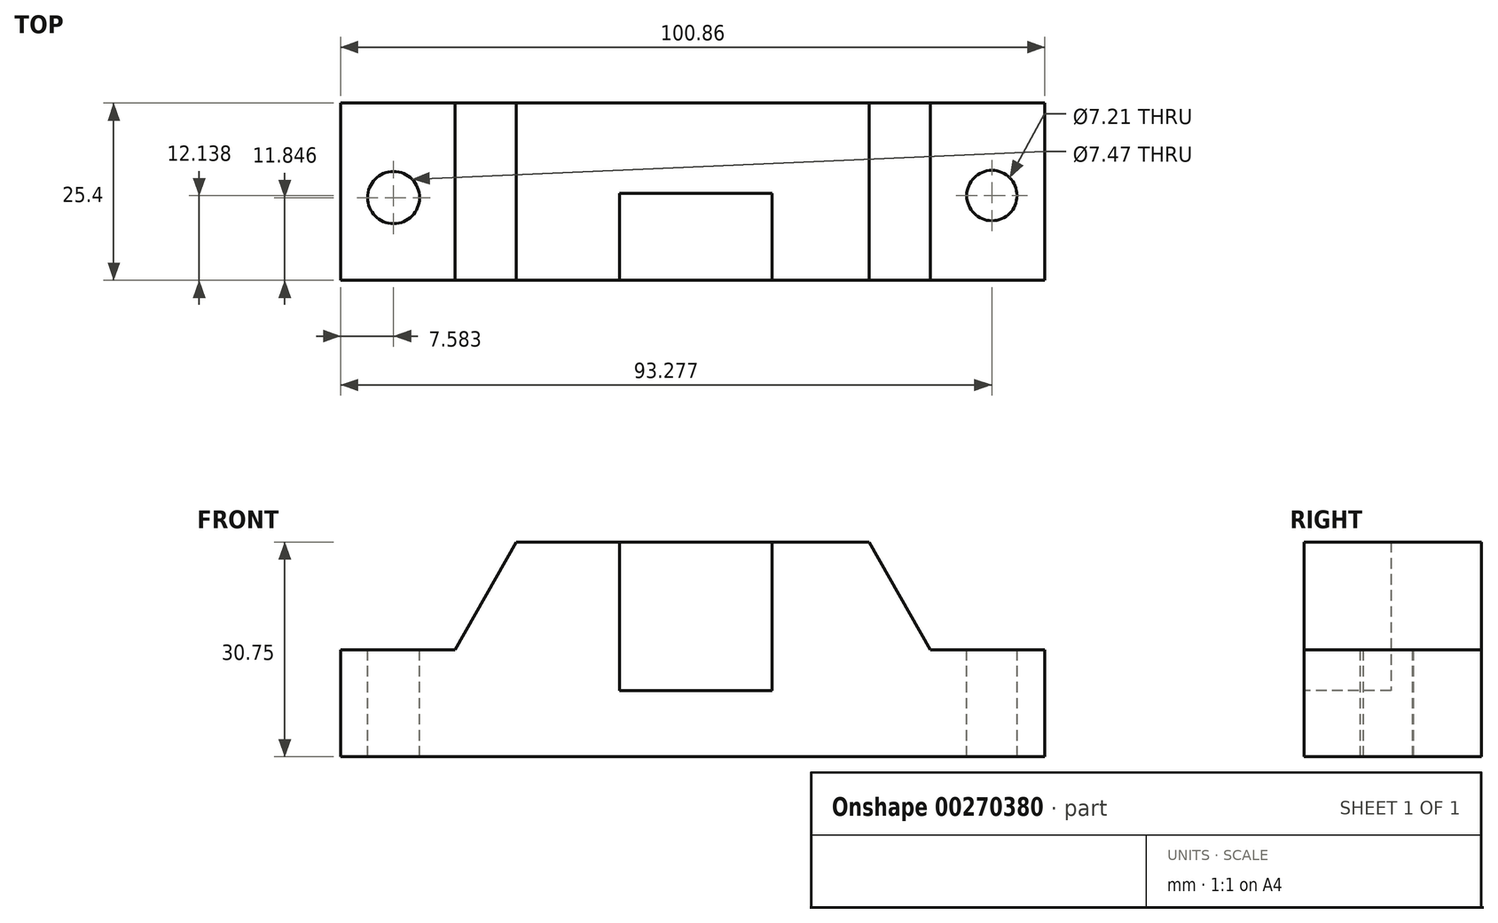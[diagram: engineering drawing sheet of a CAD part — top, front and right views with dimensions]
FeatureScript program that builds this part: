
annotation { "Feature Type Name" : "Feature", "Feature Type Description" : "" }
export const myFeature = defineFeature(function(context is Context, id is Id, definition is map)
    precondition{}
    {
        {
            var Q0;
            Q0=qCreatedBy(makeId("Front.planeOp"),FACE);
            var sketch = newSketch(context, id + "F0", { "sketchPlane" : qUnion([Q0])});
            skLineSegment(sketch, "E0", {"start": v(0, 30.75) * mm, "end": v(25.28, 30.75) * mm});
            skLineSegment(sketch, "E1", {"start": v(25.28, 30.75) * mm, "end": v(34.03, 15.3) * mm});
            skLineSegment(sketch, "E2", {"start": v(34.03, 15.3) * mm, "end": v(50.43, 15.3) * mm});
            skLineSegment(sketch, "E3", {"start": v(50.43, 15.3) * mm, "end": v(50.43, 0) * mm});
            skLineSegment(sketch, "E4", {"start": v(50.43, 0) * mm, "end": v(0, 0) * mm});
            skLineSegment(sketch, "E5", {"start": v(0, 0) * mm, "end": v(0, 30.75) * mm});
            skLineSegment(sketch, "E6.MirrorCS", {"start": v(0, 30.75) * mm, "end": v(-25.28, 30.75) * mm});
            skLineSegment(sketch, "E7.MirrorCS", {"start": v(-25.28, 30.75) * mm, "end": v(-34.03, 15.3) * mm});
            skLineSegment(sketch, "E8.MirrorCS", {"start": v(-34.03, 15.3) * mm, "end": v(-50.43, 15.3) * mm});
            skLineSegment(sketch, "E9.MirrorCS", {"start": v(-50.43, 15.3) * mm, "end": v(-50.43, 0) * mm});
            skLineSegment(sketch, "E10.MirrorCS", {"start": v(-50.43, 0) * mm, "end": v(0, 0) * mm});
            skSolve(sketch);
        }
        {
            var Q0;
            Q0 = qSketchRegion(id + "F0", true);
            extrude(context, id + "F1", {"entities" : qUnion([Q0]), "depth" : 25.4 * mm});
        }
        {
            var Q0;
            Q0=makeQuery(id+"F1.opExtrude","CAP_FACE",FACE,{"disambiguationData":[OSD([sQuery(id+"F0.wireOp",EDGE,"E0"),sQuery(id+"F0.wireOp",EDGE,"E1"),sQuery(id+"F0.wireOp",EDGE,"E2"),sQuery(id+"F0.wireOp",EDGE,"E3"),sQuery(id+"F0.wireOp",EDGE,"E4"),sQuery(id+"F0.wireOp",EDGE,"E6.MirrorCS"),sQuery(id+"F0.wireOp",EDGE,"E7.MirrorCS"),sQuery(id+"F0.wireOp",EDGE,"E8.MirrorCS"),sQuery(id+"F0.wireOp",EDGE,"E9.MirrorCS"),sQuery(id+"F0.wireOp",EDGE,"E10.MirrorCS")])],"isStart":false});
            var sketch = newSketch(context, id + "F2", { "sketchPlane" : qUnion([Q0])});
            skLineSegment(sketch, "E11", {"start": v(-10.5, 31.92) * mm, "end": v(-10.5, 9.47) * mm});
            skLineSegment(sketch, "E12", {"start": v(-10.5, 9.47) * mm, "end": v(11.37, 9.47) * mm});
            skLineSegment(sketch, "E13", {"start": v(11.37, 9.47) * mm, "end": v(11.37, 31.92) * mm});
            skLineSegment(sketch, "E14", {"start": v(-10.5, 31.92) * mm, "end": v(11.37, 31.92) * mm});
            skSolve(sketch);
        }
        {
            var Q0;
            Q0 = qSketchRegion(id + "F2", true);
            extrude(context, id + "F3", {"entities" : qUnion([Q0]), "operationType" : NewBodyOperationType.REMOVE, "oppositeDirection" : true, "depth" : 12.45 * mm});
        }
        {
            var Q0;
            Q0=makeQuery(id+"F1.opExtrude","SWEPT_FACE",FACE,{"disambiguationData":[OSD([sQuery(id+"F0.wireOp",EDGE,"E2")])]});
            var sketch = newSketch(context, id + "F4", { "sketchPlane" : qUnion([Q0])});
            skCircle(sketch, "E15", {"center": v(-42.85, -13.55) * mm, "radius": 3.73 * mm});
            skCircle(sketch, "E16", {"center": v(42.85, -13.26) * mm, "radius": 3.6 * mm});
            skSolve(sketch);
        }
        {
            var Q0;
            Q0 = qSketchRegion(id + "F4", true);
            extrude(context, id + "F5", {"entities" : qUnion([Q0]), "operationType" : NewBodyOperationType.REMOVE, "oppositeDirection" : true, "depth" : 25.4 * mm});
        }
    });
